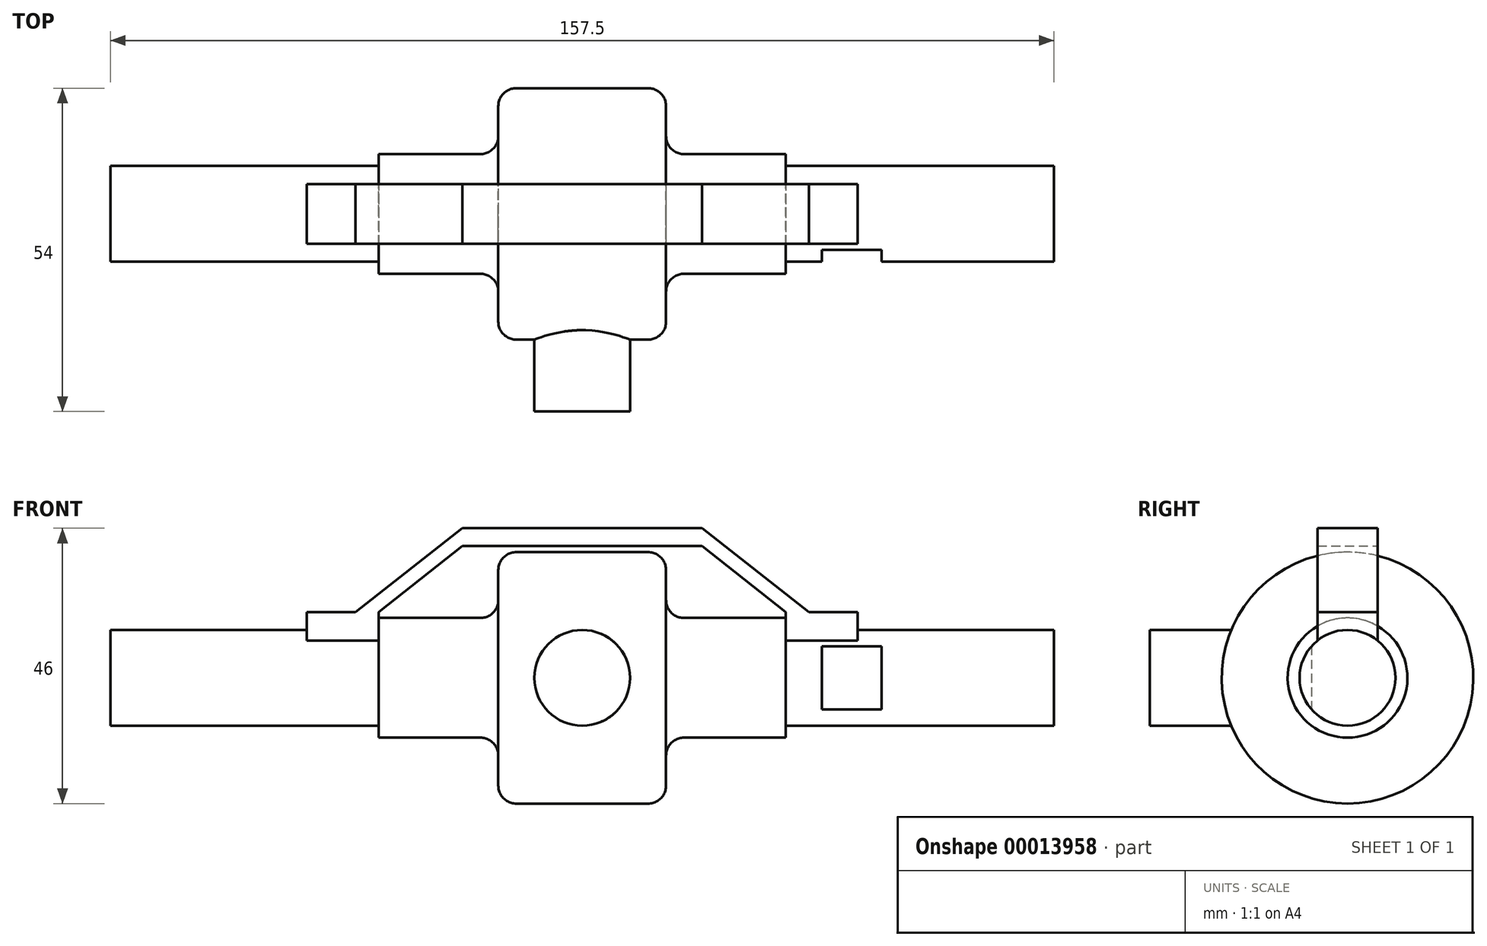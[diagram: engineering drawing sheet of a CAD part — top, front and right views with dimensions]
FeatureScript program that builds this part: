
annotation { "Feature Type Name" : "Feature", "Feature Type Description" : "" }
export const myFeature = defineFeature(function(context is Context, id is Id, definition is map)
    precondition{}
    {
        {
            var Q0;
            Q0=qCreatedBy(makeId("Front.planeOp"),FACE);
            var sketch = newSketch(context, id + "F0", { "sketchPlane" : qUnion([Q0])});
            skPoint(sketch, "E0", {"position": v(0, 0) * mm});
            skLineSegment(sketch, "E1", {"start": v(-78.75, 0) * mm, "end": v(-78.75, 8) * mm});
            skLineSegment(sketch, "E2", {"start": v(-78.75, 8) * mm, "end": v(-34, 8) * mm});
            skLineSegment(sketch, "E3", {"start": v(-34, 8) * mm, "end": v(-34, 10) * mm});
            skLineSegment(sketch, "E4", {"start": v(-34, 10) * mm, "end": v(-14, 10) * mm});
            skLineSegment(sketch, "E5", {"start": v(-14, 10) * mm, "end": v(-14, 21) * mm});
            skLineSegment(sketch, "E6", {"start": v(-14, 21) * mm, "end": v(14, 21) * mm});
            skLineSegment(sketch, "E7", {"start": v(14, 21) * mm, "end": v(14, 10) * mm});
            skLineSegment(sketch, "E8", {"start": v(14, 10) * mm, "end": v(34, 10) * mm});
            skLineSegment(sketch, "E9", {"start": v(34, 10) * mm, "end": v(34, 8) * mm});
            skLineSegment(sketch, "E10", {"start": v(34, 8) * mm, "end": v(78.75, 8) * mm});
            skLineSegment(sketch, "E11", {"start": v(78.75, 8) * mm, "end": v(78.75, 0) * mm});
            skPoint(sketch, "E12", {"position": v(0, 21) * mm});
            skLineSegment(sketch, "E13", {"start": v(-78.75, 0) * mm, "end": v(78.75, 0) * mm});
            skSolve(sketch);
        }
        {
            var Q0;
            Q0=qCreatedBy(makeId("Front.planeOp"),FACE);
            var sketch = newSketch(context, id + "F1", { "sketchPlane" : qUnion([Q0])});
            skLineSegment(sketch, "E14", {"start": v(-83.19, 0) * mm, "end": v(86.25, 0) * mm});
            skSolve(sketch);
        }
        {
            var Q0;
            Q0 = qSketchRegion(id + "F0", true);
            var Q1;
            Q1=sQuery(id+"F1.wireOp",EDGE,"E14");
            revolve(context, id + "F2", {"entities" : qUnion([Q0]), "axis" : qUnion([Q1]), "revolveType" : RevolveType.FULL});
        }
        {
            var Q0;
            Q0=qCreatedBy(makeId("Front.planeOp"),FACE);
            cPlane(context, id + "F3", {"entities" : qUnion([Q0]), "cplaneType" : CPlaneType.OFFSET, "offset" : 33 * mm, "width" : 150 * mm, "height" : 150 * mm});
        }
        {
            var Q0;
            Q0=qCreatedBy(id+"F3.planeOp",FACE);
            var sketch = newSketch(context, id + "F4", { "sketchPlane" : qUnion([Q0])});
            skCircle(sketch, "E15", {"center": v(0, 0) * mm, "radius": 8 * mm});
            skSolve(sketch);
        }
        {
            var Q0;
            Q0=makeQuery(id+"F4.imprint","IMPRINT",FACE,{"disambiguationData":[TD([[makeQuery(id+"F4.imprint","IMPRINT",EDGE,{"derivedFrom":sQuery(id+"F4.wireOp",EDGE,"E15")}),1.0]])]});
            var Q1;
            Q1=makeQuery(id+"F2.opRevolve","SWEPT_BODY",BODY,{"disambiguationData":[OSD([sQuery(id+"F0.wireOp",EDGE,"E1"),sQuery(id+"F0.wireOp",EDGE,"E2"),sQuery(id+"F0.wireOp",EDGE,"E3"),sQuery(id+"F0.wireOp",EDGE,"E4"),sQuery(id+"F0.wireOp",EDGE,"E5"),sQuery(id+"F0.wireOp",EDGE,"E6"),sQuery(id+"F0.wireOp",EDGE,"E7"),sQuery(id+"F0.wireOp",EDGE,"E8"),sQuery(id+"F0.wireOp",EDGE,"E9"),sQuery(id+"F0.wireOp",EDGE,"E10"),sQuery(id+"F0.wireOp",EDGE,"E11"),sQuery(id+"F0.wireOp",EDGE,"E13")])]});
            extrude(context, id + "F5", {"entities" : qUnion([Q0]), "operationType" : NewBodyOperationType.ADD, "endBound" : BoundingType.UP_TO_BODY, "oppositeDirection" : true, "endBoundEntityBody" : qUnion([Q1]), "depth" : 25 * mm});
        }
        {
            var Q0;
            Q0=makeQuery(id+"F2.opRevolve","SWEPT_EDGE",EDGE,{"disambiguationData":[OSD([sQuery(id+"F0.wireOp",EDGE,"E4"),sQuery(id+"F0.wireOp",EDGE,"E5")])]});
            var Q1;
            Q1=makeQuery(id+"F2.opRevolve","SWEPT_EDGE",EDGE,{"disambiguationData":[OSD([sQuery(id+"F0.wireOp",EDGE,"E5"),sQuery(id+"F0.wireOp",EDGE,"E6")])]});
            var Q2;
            Q2=makeQuery(id+"F2.opRevolve","SWEPT_EDGE",EDGE,{"disambiguationData":[OSD([sQuery(id+"F0.wireOp",EDGE,"E6"),sQuery(id+"F0.wireOp",EDGE,"E7")])]});
            var Q3;
            Q3=makeQuery(id+"F5.opExtrude","TWEAK_EDGE",EDGE,{"derivedFrom":[makeQuery(id+"F2.opRevolve","SWEPT_FACE",FACE,{"disambiguationData":[OSD([sQuery(id+"F0.wireOp",EDGE,"E6")])]}),makeQuery(id+"F4.imprint","IMPRINT",EDGE,{"derivedFrom":sQuery(id+"F4.wireOp",EDGE,"E15")})]});
            var Q4;
            Q4=makeQuery(id+"F2.opRevolve","SWEPT_EDGE",EDGE,{"disambiguationData":[OSD([sQuery(id+"F0.wireOp",EDGE,"E7"),sQuery(id+"F0.wireOp",EDGE,"E8")])]});
            fillet(context, id + "F6", {"entities" : qUnion([Q0, Q1, Q2, Q3, Q4]), "radius" : 3 * mm, "tangentPropagation" : true, "allowEdgeOverflow" : false});
        }
        {
            var Q0;
            Q0=qCreatedBy(makeId("Front.planeOp"),FACE);
            var sketch = newSketch(context, id + "F7", { "sketchPlane" : qUnion([Q0])});
            skLineSegment(sketch, "E16", {"start": v(-34, 6) * mm, "end": v(-34, 11) * mm});
            skLineSegment(sketch, "E17", {"start": v(-34, 11) * mm, "end": v(-20, 22) * mm});
            skLineSegment(sketch, "E18", {"start": v(-20, 22) * mm, "end": v(20, 22) * mm});
            skLineSegment(sketch, "E19", {"start": v(20, 22) * mm, "end": v(34, 11) * mm});
            skLineSegment(sketch, "E20", {"start": v(34, 11) * mm, "end": v(34, 6) * mm});
            skLineSegment(sketch, "E21", {"start": v(34, 6) * mm, "end": v(46, 6) * mm});
            skLineSegment(sketch, "E22", {"start": v(46, 6) * mm, "end": v(46, 11) * mm});
            skLineSegment(sketch, "E23", {"start": v(46, 11) * mm, "end": v(37.82, 11) * mm});
            skLineSegment(sketch, "E24", {"start": v(37.82, 11) * mm, "end": v(20, 25) * mm});
            skLineSegment(sketch, "E25", {"start": v(20, 25) * mm, "end": v(-20, 25) * mm});
            skLineSegment(sketch, "E26", {"start": v(-20, 25) * mm, "end": v(-37.82, 11) * mm});
            skLineSegment(sketch, "E27", {"start": v(-37.82, 11) * mm, "end": v(-46, 11) * mm});
            skLineSegment(sketch, "E28", {"start": v(-46, 11) * mm, "end": v(-46, 6) * mm});
            skLineSegment(sketch, "E29", {"start": v(-46, 6) * mm, "end": v(-34, 6) * mm});
            skPoint(sketch, "E30", {"position": v(0, 25) * mm});
            skPoint(sketch, "E31", {"position": v(0, 22) * mm});
            skSolve(sketch);
        }
        {
            var Q0;
            Q0 = qSketchRegion(id + "F7", true);
            extrude(context, id + "F8", {"entities" : qUnion([Q0]), "operationType" : NewBodyOperationType.ADD, "depth" : 10 * mm, "symmetric" : true});
        }
        {
            var Q0;
            Q0=qCreatedBy(makeId("Right.planeOp"),FACE);
            cPlane(context, id + "F9", {"entities" : qUnion([Q0]), "cplaneType" : CPlaneType.OFFSET, "offset" : 40 * mm, "width" : 150 * mm, "height" : 150 * mm});
        }
        {
            var Q0;
            Q0=qCreatedBy(id+"F9.planeOp",FACE);
            var sketch = newSketch(context, id + "F10", { "sketchPlane" : qUnion([Q0])});
            skLineSegment(sketch, "E32", {"start": v(-6, 5.3) * mm, "end": v(-6, -5.3) * mm});
            skArc(sketch, "E33", {"start": v(-6, 5.3) * mm, "mid": v(-8, 0) * mm, "end": v(-6, -5.3) * mm});
            skSolve(sketch);
        }
        {
            var Q0;
            Q0 = qSketchRegion(id + "F10", true);
            extrude(context, id + "F11", {"entities" : qUnion([Q0]), "operationType" : NewBodyOperationType.REMOVE, "depth" : 10 * mm});
        }
    });
